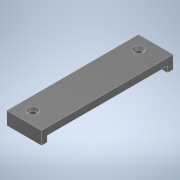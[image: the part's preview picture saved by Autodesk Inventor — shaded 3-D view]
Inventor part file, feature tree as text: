
AUTODESK INVENTOR PART (.ipt)
format: ipt  version: 2022 (Build 260153000, 153)  size: 123,904 bytes
history: native  units: in
note: dims shown in document units (in); Inventor stores cm internally (conversion verified against a paired STEP export)
features: sketch x3, extrude x2, hole x1
ambient origin geometry x8: Origin, YZ Plane, XZ Plane, XY Plane, X Axis, Y Axis, Z Axis, Center Point
bodies: Solid1 (feature_tree)
feature tree (6):
  extrude  "Extrusion1"  Depth=1.9in
  extrude  "Extrusion2"  Depth=0.0846in
  hole  "Hole1"  [1 undecoded]
  sketch  "Sketch1"  dims[d0=0.5in d1=1.9in]
  sketch  "Sketch2"  dims[d2=0.1875in d3=0.0in d4=0.0846in]
  sketch  "Sketch3"  dims[d5=1.7362in d6=0.125in d7=0.0in d11=0.081in d12=0.75in d13=0.146in d14=0.188in d15=0.5635in d16=1.0in d17=0.8108in d18=0.1875in d19=0.1875in]
note: 1 required parameter value undecoded (feature->parameter linkage not recoverable at this tier; creation-order binding heuristic only, values carry confidence <= 0.55)
